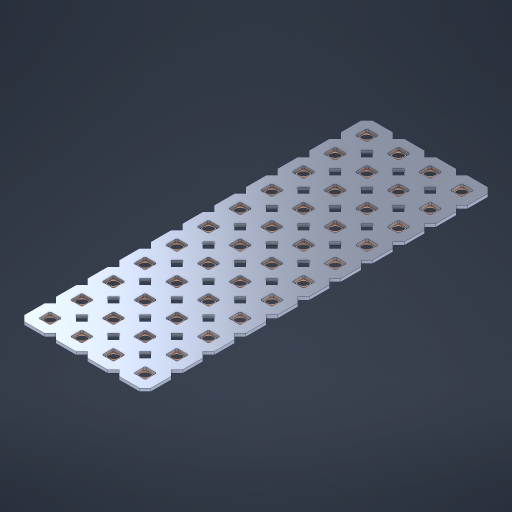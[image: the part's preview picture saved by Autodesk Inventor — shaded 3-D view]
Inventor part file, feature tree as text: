
AUTODESK INVENTOR PART (.ipt)
format: ipt  version: 2023 (Build 270158000, 158)  size: 766,976 bytes
history: native  units: in
note: dims shown in document units (in); Inventor stores cm internally (conversion verified against a paired STEP export)
features: other x45, extrude x43, sketch x2, pattern_linear x1
ambient origin geometry x8: Origin, YZ Plane, XZ Plane, XY Plane, X Axis, Y Axis, Z Axis, Center Point
bodies: Solid1 (feature_tree), Body (feature_tree)
feature tree (91):
  pattern_linear  "Rectangular Pattern1"  Spacing1=0.09in  [1 undecoded]
  sketch  "Sketch1"  dims[d1=0.5in]
  sketch  "Sketch2"  dims[d2=0.182in d3=0.09in d4=0.09in d5=0.09in d6=0.09in d7=0.09in d8=0.09in d9=0.09in d10=0.09in d11=0.02in d13=0.0in d14=0.172in d15=0.0625in d16=0.0in d19=0.5in d22=0.5in]
  other  "Srf1"
  other  "Srf126"
  other  "Srf127"
  other  "Srf128"
  other  "Srf129"
  other  "Srf130"
  other  "Srf131"
  other  "Srf250"
  other  "Srf251"
  other  "Srf252"
  other  "Srf253"
  other  "Srf268"
  other  "Srf269"
  other  "Srf270"
  other  "Srf271"
  other  "Srf272"
  other  "Srf273"
  other  "Srf274"
  other  "Srf275"
  other  "Srf276"
  other  "Srf277"
  other  "Srf278"
  other  "Srf293"
  other  "Srf294"
  other  "Srf295"
  other  "Srf296"
  other  "Srf297"
  other  "Srf298"
  other  "Srf299"
  other  "Srf300"
  other  "Srf301"
  other  "Srf302"
  other  "Srf303"
  other  "Srf318"
  other  "Srf319"
  other  "Srf320"
  other  "Srf321"
  other  "Srf322"
  other  "Srf323"
  other  "Srf324"
  other  "Srf325"
  other  "Srf326"
  other  "Srf327"
  other  "Srf328"
  other  "Circle"
  extrude  "ExtrusionSrf126"  Depth=0.09in
  extrude  "ExtrusionSrf127"  Depth=0.09in
  extrude  "ExtrusionSrf128"  Depth=0.09in
  extrude  "ExtrusionSrf129"  Depth=0.09in
  extrude  "ExtrusionSrf130"  Depth=0.09in
  extrude  "ExtrusionSrf131"  Depth=0.09in
  extrude  "ExtrusionSrf250"  Depth=0.09in
  extrude  "ExtrusionSrf251"  Depth=0.02in
  extrude  "ExtrusionSrf252"  TaperAngle=0.0deg  [1 undecoded]
  extrude  "ExtrusionSrf253"  Depth=0.5in
  extrude  "ExtrusionSrf268"  Depth=0.5in TaperAngle=0.0deg
  extrude  "ExtrusionSrf269"  Depth=0.5in
  extrude  "ExtrusionSrf270"  Depth=0.5in
  extrude  "ExtrusionSrf271"  [1 undecoded]
  extrude  "ExtrusionSrf272"  [1 undecoded]
  extrude  "ExtrusionSrf273"  [1 undecoded]
  extrude  "ExtrusionSrf274"  [1 undecoded]
  extrude  "ExtrusionSrf275"  [1 undecoded]
  extrude  "ExtrusionSrf276"  [1 undecoded]
  extrude  "ExtrusionSrf277"  [1 undecoded]
  extrude  "ExtrusionSrf278"  [1 undecoded]
  extrude  "ExtrusionSrf293"  [1 undecoded]
  extrude  "ExtrusionSrf294"  [1 undecoded]
  extrude  "ExtrusionSrf295"  [1 undecoded]
  extrude  "ExtrusionSrf296"  [1 undecoded]
  extrude  "ExtrusionSrf297"  [1 undecoded]
  extrude  "ExtrusionSrf298"  [1 undecoded]
  extrude  "ExtrusionSrf299"  [1 undecoded]
  extrude  "ExtrusionSrf300"  [1 undecoded]
  extrude  "ExtrusionSrf301"  [1 undecoded]
  extrude  "ExtrusionSrf302"  [1 undecoded]
  extrude  "ExtrusionSrf303"  [1 undecoded]
  extrude  "ExtrusionSrf318"  [1 undecoded]
  extrude  "ExtrusionSrf319"  [1 undecoded]
  extrude  "ExtrusionSrf320"  [1 undecoded]
  extrude  "ExtrusionSrf321"  [1 undecoded]
  extrude  "ExtrusionSrf322"  [1 undecoded]
  extrude  "ExtrusionSrf323"  [1 undecoded]
  extrude  "ExtrusionSrf324"  [1 undecoded]
  extrude  "ExtrusionSrf325"  [1 undecoded]
  extrude  "ExtrusionSrf326"  [1 undecoded]
  extrude  "ExtrusionSrf327"  [1 undecoded]
  extrude  "ExtrusionSrf328"  [1 undecoded]
note: 32 required parameter values undecoded (feature->parameter linkage not recoverable at this tier; creation-order binding heuristic only, values carry confidence <= 0.55)
